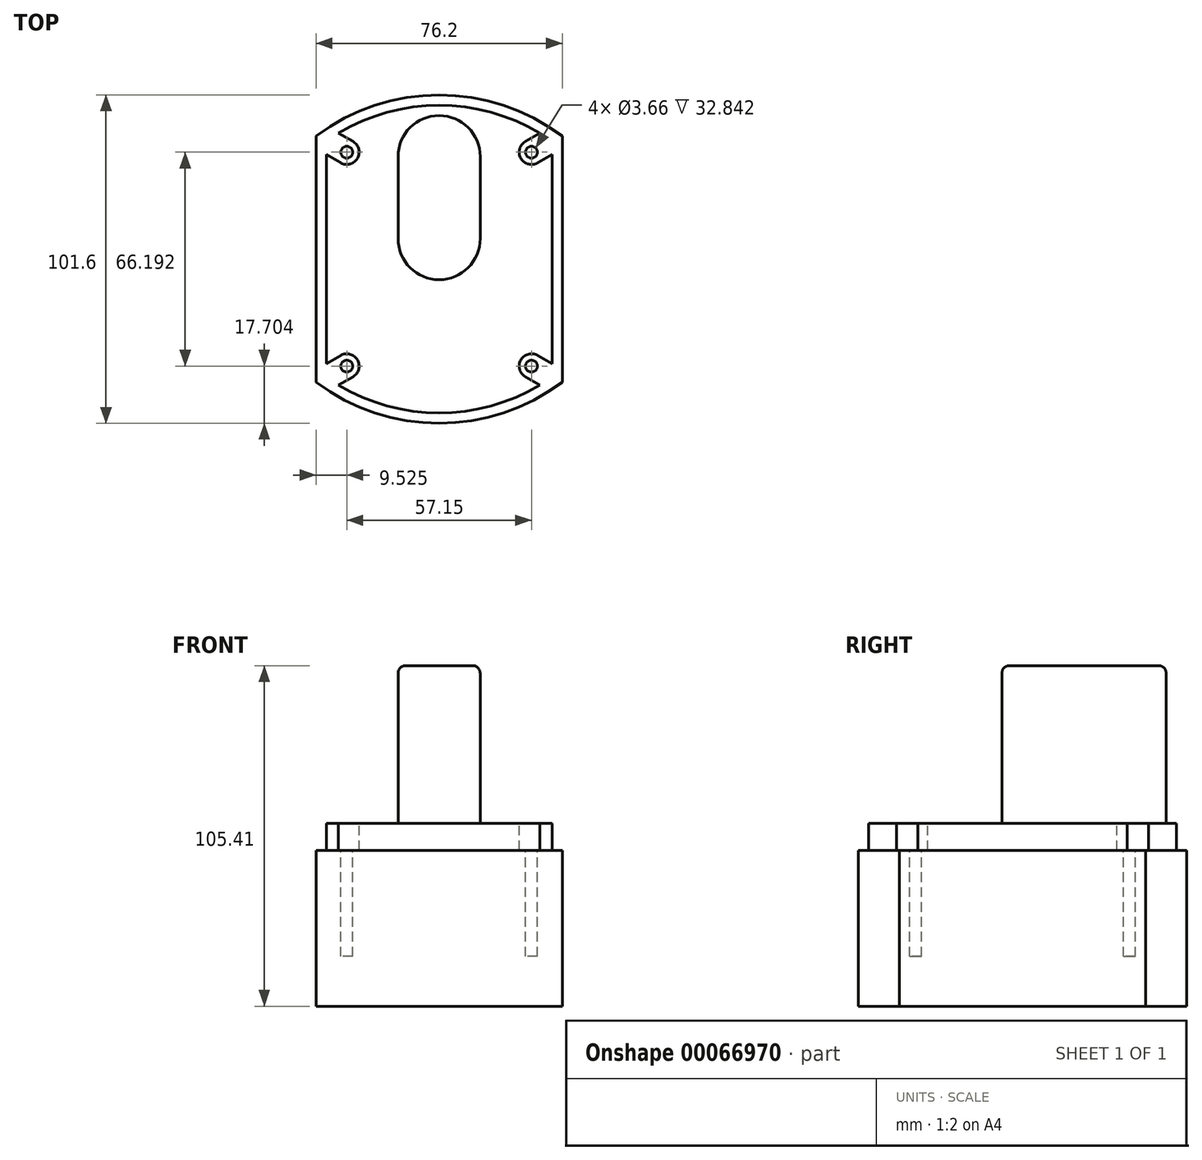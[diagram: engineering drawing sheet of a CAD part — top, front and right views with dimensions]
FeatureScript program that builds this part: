
annotation { "Feature Type Name" : "Feature", "Feature Type Description" : "" }
export const myFeature = defineFeature(function(context is Context, id is Id, definition is map)
    precondition{}
    {
        {
            var Q0;
            Q0=qCreatedBy(makeId("Top.planeOp"),FACE);
            var sketch = newSketch(context, id + "F0", { "sketchPlane" : qUnion([Q0])});
            skLineSegment(sketch, "E0.rect.bottom", {"start": v(-38.1, -38.1) * mm, "end": v(38.1, -38.1) * mm, "construction": true});
            skLineSegment(sketch, "E0.rect.top", {"start": v(-38.1, 38.1) * mm, "end": v(38.1, 38.1) * mm, "construction": true});
            skLineSegment(sketch, "E0.rect.left", {"start": v(-38.1, -38.1) * mm, "end": v(-38.1, 38.1) * mm});
            skLineSegment(sketch, "E0.rect.right", {"start": v(38.1, -38.1) * mm, "end": v(38.1, 38.1) * mm});
            skPoint(sketch, "E0.rect.middle", {"position": v(0, 0) * mm});
            skLineSegment(sketch, "E1", {"start": v(0, 38.1) * mm, "end": v(0, 50.8) * mm, "construction": true});
            skPoint(sketch, "E1.endSnap0", {"position": v(0, 38.1) * mm});
            skArc(sketch, "E2", {"start": v(38.1, 38.1) * mm, "mid": v(0, 50.8) * mm, "end": v(-38.1, 38.1) * mm});
            skLineSegment(sketch, "E3", {"start": v(-38.1, 0) * mm, "end": v(38.1, 0) * mm, "construction": true});
            skArc(sketch, "E4.MirrorCS", {"start": v(38.1, -38.1) * mm, "mid": v(0, -50.8) * mm, "end": v(-38.1, -38.1) * mm});
            skSolve(sketch);
        }
        {
            var Q0;
            Q0 = qSketchRegion(id + "F0", true);
            extrude(context, id + "F1", {"entities" : qUnion([Q0]), "oppositeDirection" : true, "depth" : 48.26 * mm});
        }
        {
            var Q0;
            Q0=makeQuery(id+"F1.opExtrude","CAP_FACE",FACE,{"disambiguationData":[OSD([sQuery(id+"F0.wireOp",EDGE,"E0.rect.left"),sQuery(id+"F0.wireOp",EDGE,"E0.rect.right"),sQuery(id+"F0.wireOp",EDGE,"E2"),sQuery(id+"F0.wireOp",EDGE,"E4.MirrorCS")])],"isStart":true});
            var sketch = newSketch(context, id + "F2", { "sketchPlane" : qUnion([Q0])});
            skLineSegment(sketch, "E5.0.0", {"start": v(-38.1, 38.1) * mm, "end": v(-38.1, -38.1) * mm});
            skArc(sketch, "E5.0.1", {"start": v(-38.1, -38.1) * mm, "mid": v(0, -50.8) * mm, "end": v(38.1, -38.1) * mm, "construction": true});
            skLineSegment(sketch, "E5.0.2", {"start": v(38.1, -38.1) * mm, "end": v(38.1, 38.1) * mm, "construction": true});
            skArc(sketch, "E5.0.3", {"start": v(38.1, 38.1) * mm, "mid": v(0, 50.8) * mm, "end": v(-38.1, 38.1) * mm, "construction": true});
            skLineSegment(sketch, "E6.0", {"start": v(-34.93, 36.49) * mm, "end": v(-34.93, -36.49) * mm});
            skArc(sketch, "E6.1", {"start": v(34.92, 36.49) * mm, "mid": v(0, 47.63) * mm, "end": v(-34.93, 36.49) * mm});
            skLineSegment(sketch, "E6.2", {"start": v(34.93, -36.49) * mm, "end": v(34.93, 36.49) * mm});
            skArc(sketch, "E6.3", {"start": v(-34.93, -36.49) * mm, "mid": v(0, -47.63) * mm, "end": v(34.93, -36.49) * mm});
            skSolve(sketch);
        }
        {
            var Q0;
            Q0 = qSketchRegion(id + "F2", true);
            extrude(context, id + "F3", {"entities" : qUnion([Q0]), "operationType" : NewBodyOperationType.ADD, "depth" : 8.38 * mm});
        }
        {
            var Q0;
            Q0=makeQuery(id+"F3.opExtrude","CAP_FACE",FACE,{"disambiguationData":[OSD([sQuery(id+"F2.wireOp",EDGE,"E6.0"),sQuery(id+"F2.wireOp",EDGE,"E6.1"),sQuery(id+"F2.wireOp",EDGE,"E6.2"),sQuery(id+"F2.wireOp",EDGE,"E6.3")])],"isStart":false});
            var sketch = newSketch(context, id + "F4", { "sketchPlane" : qUnion([Q0])});
            skLineSegment(sketch, "E7.rect.bottom", {"start": v(-28.58, -33.1) * mm, "end": v(28.57, -33.1) * mm, "construction": true});
            skLineSegment(sketch, "E7.rect.top", {"start": v(-28.58, 33.1) * mm, "end": v(28.58, 33.1) * mm, "construction": true});
            skLineSegment(sketch, "E7.rect.left", {"start": v(-28.58, -33.1) * mm, "end": v(-28.58, 33.1) * mm, "construction": true});
            skLineSegment(sketch, "E7.rect.right", {"start": v(28.57, -33.1) * mm, "end": v(28.58, 33.1) * mm, "construction": true});
            skPoint(sketch, "E7.rect.middle", {"position": v(0, 0) * mm});
            skLineSegment(sketch, "E8", {"start": v(-28.58, -33.1) * mm, "end": v(-50.57, -45.8) * mm, "construction": true});
            skArc(sketch, "E9.0.startCap", {"start": v(-30.48, -29.8) * mm, "mid": v(-25.28, -31.2) * mm, "end": v(-26.67, -36.4) * mm});
            skArc(sketch, "E9.0.endCap", {"start": v(-48.67, -49.1) * mm, "mid": v(-53.87, -47.7) * mm, "end": v(-52.48, -42.5) * mm});
            skLineSegment(sketch, "E9.0.left", {"start": v(-26.67, -36.4) * mm, "end": v(-48.67, -49.1) * mm});
            skLineSegment(sketch, "E9.0.right", {"start": v(-30.48, -29.8) * mm, "end": v(-52.48, -42.5) * mm});
            skLineSegment(sketch, "E10", {"start": v(-28.58, 0) * mm, "end": v(28.58, 0) * mm, "construction": true});
            skLineSegment(sketch, "E11", {"start": v(0, 33.1) * mm, "end": v(0, -33.1) * mm, "construction": true});
            skArc(sketch, "E12.MirrorCS", {"start": v(30.48, -29.8) * mm, "mid": v(25.28, -31.2) * mm, "end": v(26.67, -36.4) * mm});
            skLineSegment(sketch, "E13.MirrorCS", {"start": v(30.48, -29.8) * mm, "end": v(52.48, -42.5) * mm});
            skLineSegment(sketch, "E14.MirrorCS", {"start": v(26.67, -36.4) * mm, "end": v(48.67, -49.1) * mm});
            skArc(sketch, "E15.MirrorCS", {"start": v(48.67, -49.1) * mm, "mid": v(53.87, -47.7) * mm, "end": v(52.48, -42.5) * mm});
            skArc(sketch, "E16.MirrorCS", {"start": v(-30.48, 29.8) * mm, "mid": v(-25.28, 31.2) * mm, "end": v(-26.67, 36.4) * mm});
            skLineSegment(sketch, "E17.MirrorCS", {"start": v(-30.48, 29.8) * mm, "end": v(-52.48, 42.5) * mm});
            skArc(sketch, "E18.MirrorCS", {"start": v(-48.67, 49.1) * mm, "mid": v(-53.87, 47.7) * mm, "end": v(-52.48, 42.5) * mm});
            skLineSegment(sketch, "E19.MirrorCS", {"start": v(-26.67, 36.4) * mm, "end": v(-48.67, 49.1) * mm});
            skLineSegment(sketch, "E20.MirrorCS", {"start": v(30.48, 29.8) * mm, "end": v(52.48, 42.5) * mm});
            skArc(sketch, "E21.MirrorCS", {"start": v(30.48, 29.8) * mm, "mid": v(25.28, 31.2) * mm, "end": v(26.67, 36.4) * mm});
            skLineSegment(sketch, "E22.MirrorCS", {"start": v(26.67, 36.4) * mm, "end": v(48.67, 49.1) * mm});
            skArc(sketch, "E23.MirrorCS", {"start": v(48.67, 49.1) * mm, "mid": v(53.87, 47.7) * mm, "end": v(52.48, 42.5) * mm});
            skCircle(sketch, "E24", {"center": v(-28.58, 33.1) * mm, "radius": 1.83 * mm, "construction": true});
            skCircle(sketch, "E25", {"center": v(28.58, 33.1) * mm, "radius": 1.83 * mm, "construction": true});
            skCircle(sketch, "E26", {"center": v(28.57, -33.1) * mm, "radius": 1.83 * mm, "construction": true});
            skCircle(sketch, "E27", {"center": v(-28.58, -33.1) * mm, "radius": 1.83 * mm, "construction": true});
            skSolve(sketch);
        }
        {
            var Q0;
            Q0 = qSketchRegion(id + "F4", true);
            var Q1;
            Q1=makeQuery(id+"F1.opExtrude","CAP_FACE",FACE,{"disambiguationData":[OSD([sQuery(id+"F0.wireOp",EDGE,"E0.rect.left"),sQuery(id+"F0.wireOp",EDGE,"E0.rect.right"),sQuery(id+"F0.wireOp",EDGE,"E2"),sQuery(id+"F0.wireOp",EDGE,"E4.MirrorCS")])],"isStart":true});
            extrude(context, id + "F5", {"entities" : qUnion([Q0]), "operationType" : NewBodyOperationType.REMOVE, "endBound" : BoundingType.UP_TO_SURFACE, "oppositeDirection" : true, "endBoundEntityFace" : qUnion([Q1]), "depth" : 25.4 * mm});
        }
        {
            var Q0;
            Q0=makeQuery(id+"F5.boolean.opBoolean","MERGE",FACE,{"derivedFrom":[makeQuery(id+"F1.opExtrude","CAP_FACE",FACE,{"disambiguationData":[OSD([sQuery(id+"F0.wireOp",EDGE,"E0.rect.left"),sQuery(id+"F0.wireOp",EDGE,"E0.rect.right"),sQuery(id+"F0.wireOp",EDGE,"E2"),sQuery(id+"F0.wireOp",EDGE,"E4.MirrorCS")])],"isStart":true}),makeQuery(id+"F5.opExtrude","CAP_FACE",FACE,{"disambiguationData":[OSD([sQuery(id+"F4.wireOp",EDGE,"E9.0.startCap"),sQuery(id+"F4.wireOp",EDGE,"E9.0.endCap"),sQuery(id+"F4.wireOp",EDGE,"E9.0.left"),sQuery(id+"F4.wireOp",EDGE,"E9.0.right")])],"isStart":false}),makeQuery(id+"F5.opExtrude","CAP_FACE",FACE,{"disambiguationData":[OSD([sQuery(id+"F4.wireOp",EDGE,"E12.MirrorCS"),sQuery(id+"F4.wireOp",EDGE,"E13.MirrorCS"),sQuery(id+"F4.wireOp",EDGE,"E14.MirrorCS"),sQuery(id+"F4.wireOp",EDGE,"E15.MirrorCS")])],"isStart":false}),makeQuery(id+"F5.opExtrude","CAP_FACE",FACE,{"disambiguationData":[OSD([sQuery(id+"F4.wireOp",EDGE,"E16.MirrorCS"),sQuery(id+"F4.wireOp",EDGE,"E17.MirrorCS"),sQuery(id+"F4.wireOp",EDGE,"E18.MirrorCS"),sQuery(id+"F4.wireOp",EDGE,"E19.MirrorCS")])],"isStart":false}),makeQuery(id+"F5.opExtrude","CAP_FACE",FACE,{"disambiguationData":[OSD([sQuery(id+"F4.wireOp",EDGE,"E20.MirrorCS"),sQuery(id+"F4.wireOp",EDGE,"E21.MirrorCS"),sQuery(id+"F4.wireOp",EDGE,"E22.MirrorCS"),sQuery(id+"F4.wireOp",EDGE,"E23.MirrorCS")])],"isStart":false})]});
            var sketch = newSketch(context, id + "F6", { "sketchPlane" : qUnion([Q0])});
            skCircle(sketch, "E28.0", {"center": v(28.57, -33.1) * mm, "radius": 1.83 * mm});
            skCircle(sketch, "E28.1", {"center": v(-28.58, -33.1) * mm, "radius": 1.83 * mm});
            skCircle(sketch, "E28.2", {"center": v(28.58, 33.1) * mm, "radius": 1.83 * mm});
            skCircle(sketch, "E28.3", {"center": v(-28.58, 33.1) * mm, "radius": 1.83 * mm});
            skSolve(sketch);
        }
        {
            var Q0;
            Q0 = qSketchRegion(id + "F6", true);
            extrude(context, id + "F7", {"entities" : qUnion([Q0]), "operationType" : NewBodyOperationType.REMOVE, "oppositeDirection" : true, "depth" : 32.84 * mm});
        }
        {
            var Q0;
            Q0=qCreatedBy(makeId("Top.planeOp"),FACE);
            var sketch = newSketch(context, id + "F8", { "sketchPlane" : qUnion([Q0])});
            skLineSegment(sketch, "E29", {"start": v(0, 6.35) * mm, "end": v(0, 31.75) * mm, "construction": true});
            skArc(sketch, "E30.0.startCap", {"start": v(12.7, 6.35) * mm, "mid": v(0, -6.35) * mm, "end": v(-12.7, 6.35) * mm});
            skArc(sketch, "E30.0.endCap", {"start": v(-12.7, 31.75) * mm, "mid": v(0, 44.45) * mm, "end": v(12.7, 31.75) * mm});
            skLineSegment(sketch, "E30.0.left", {"start": v(-12.7, 6.35) * mm, "end": v(-12.7, 31.75) * mm});
            skLineSegment(sketch, "E30.0.right", {"start": v(12.7, 6.35) * mm, "end": v(12.7, 31.75) * mm});
            skPoint(sketch, "E31", {"position": v(0, 19.05) * mm});
            skSolve(sketch);
        }
        {
            var Q0;
            Q0 = qSketchRegion(id + "F8", true);
            extrude(context, id + "F9", {"entities" : qUnion([Q0]), "operationType" : NewBodyOperationType.ADD, "depth" : 57.15 * mm});
        }
        {
            var Q0;
            Q0=makeQuery(id+"F9.opExtrude","CAP_EDGE",EDGE,{"disambiguationData":[OSD([sQuery(id+"F8.wireOp",EDGE,"E30.0.right")])],"isStart":false});
            fillet(context, id + "F10", {"entities" : qUnion([Q0]), "radius" : 2.3 * mm, "tangentPropagation" : true, "allowEdgeOverflow" : false});
        }
    });
